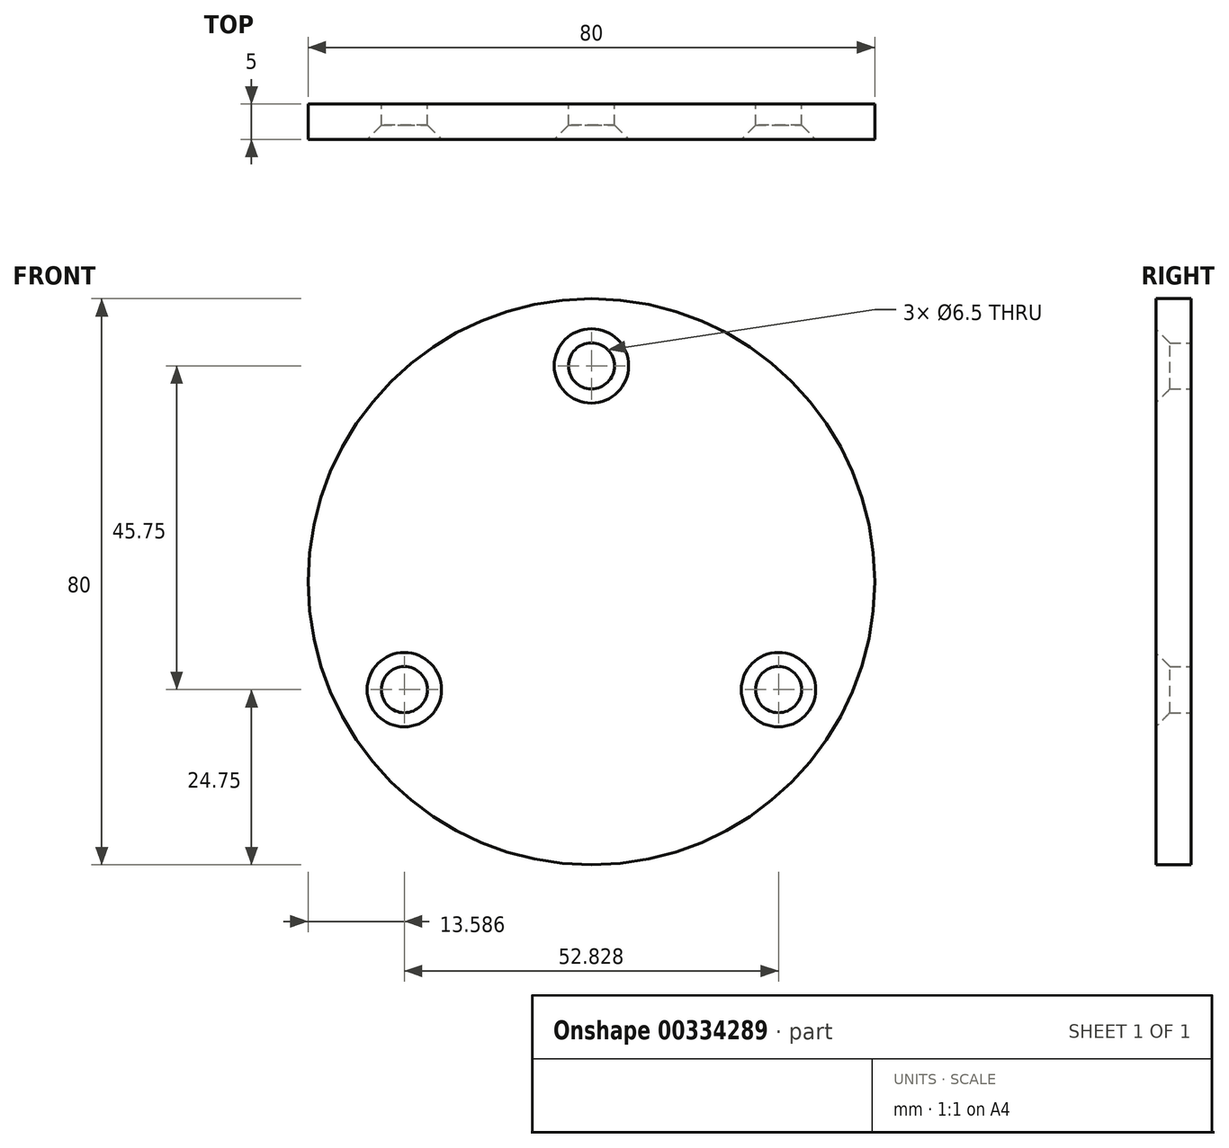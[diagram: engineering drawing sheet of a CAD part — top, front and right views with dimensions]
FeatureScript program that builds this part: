
annotation { "Feature Type Name" : "Feature", "Feature Type Description" : "" }
export const myFeature = defineFeature(function(context is Context, id is Id, definition is map)
    precondition{}
    {
        {
            var Q0;
            Q0=qCreatedBy(makeId("Front.planeOp"),FACE);
            var sketch = newSketch(context, id + "F0", { "sketchPlane" : qUnion([Q0])});
            skCircle(sketch, "E0", {"center": v(0, 0) * mm, "radius": 40 * mm});
            skCircle(sketch, "E1", {"center": v(0, 0) * mm, "radius": 30.5 * mm, "construction": true});
            skCircle(sketch, "E2", {"center": v(0, 30.5) * mm, "radius": 3.25 * mm});
            skCircle(sketch, "E3.1.0", {"center": v(-26.41, -15.25) * mm, "radius": 3.25 * mm});
            skCircle(sketch, "E3.2.0", {"center": v(26.41, -15.25) * mm, "radius": 3.25 * mm});
            skLineSegment(sketch, "E4", {"start": v(0, 30.5) * mm, "end": v(0, 0) * mm, "construction": true});
            skLineSegment(sketch, "E5", {"start": v(0, 0) * mm, "end": v(26.41, -15.25) * mm, "construction": true});
            skLineSegment(sketch, "E6", {"start": v(0, 0) * mm, "end": v(-26.41, -15.25) * mm, "construction": true});
            skSolve(sketch);
        }
        {
            var Q0;
            Q0=qSketchRegion(id+"F0",true);
            extrude(context, id + "F1", {"entities" : qUnion([Q0]), "depth" : 5 * mm});
        }
        {
            var Q0;
            Q0=makeQuery(id+"F1.opExtrude","CAP_EDGE",EDGE,{"disambiguationData":[OSD([sQuery(id+"F0.wireOp",EDGE,"E2")])],"isStart":false});
            var Q1;
            Q1=makeQuery(id+"F1.opExtrude","CAP_EDGE",EDGE,{"disambiguationData":[OSD([sQuery(id+"F0.wireOp",EDGE,"E3.2.0")])],"isStart":false});
            var Q2;
            Q2=makeQuery(id+"F1.opExtrude","CAP_EDGE",EDGE,{"disambiguationData":[OSD([sQuery(id+"F0.wireOp",EDGE,"E3.1.0")])],"isStart":false});
            chamfer(context, id + "F2", {"entities" : qUnion([Q0, Q1, Q2]), "width" : 2 * mm, "tangentPropagation" : true});
        }
    });
